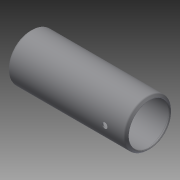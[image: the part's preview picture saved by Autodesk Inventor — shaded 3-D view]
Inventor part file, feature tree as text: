
AUTODESK INVENTOR PART (.ipt)
format: ipt  version: 2014 SP2 (Build 180246200, 246)  size: 158,208 bytes
history: native  units: in
note: dims shown in document units (in); Inventor stores cm internally (conversion verified against a paired STEP export)
features: other x42, sketch x2, revolve x1, extrude x1
ambient origin geometry x8: Origin, YZ Plane, XZ Plane, XY Plane, X Axis, Y Axis, Z Axis, Center Point
bodies: Solid1 (feature_tree)
feature tree (46):
  revolve  "Revolution1"  [1 undecoded]
  extrude  "Extrusion1"  [1 undecoded]
  other  "cp1_XY"
  other  "cp1_YZ"
  other  "cp1_ZX"
  other  "cp1_X"
  other  "cp1_Y"
  other  "cp1_Z"
  other  "cp1_Center"
  other  "cp2_XY"
  other  "cp2_YZ"
  other  "cp2_ZX"
  other  "cp2_X"
  other  "cp2_Y"
  other  "cp2_Z"
  other  "cp2_Center"
  other  "cp3_XY"
  other  "cp3_YZ"
  other  "cp3_ZX"
  other  "cp3_X"
  other  "cp3_Y"
  other  "cp3_Z"
  other  "cp3_Center"
  other  "cp4_XY"
  other  "cp4_YZ"
  other  "cp4_ZX"
  other  "cp4_X"
  other  "cp4_Y"
  other  "cp4_Z"
  other  "cp4_Center"
  other  "tube_front_XY"
  other  "tube_front_YZ"
  other  "tube_front_ZX"
  other  "tube_front_X"
  other  "tube_front_Y"
  other  "tube_front_Z"
  other  "tube_front_Center"
  other  "tube_rear_XY"
  other  "tube_rear_YZ"
  other  "tube_rear_ZX"
  other  "tube_rear_X"
  other  "tube_rear_Y"
  other  "tube_rear_Z"
  other  "tube_rear_Center"
  sketch  "Sketch_1"  dims[d0=360.0deg d1=0.4038in d2=0.0in]
  sketch  "Sketch_7"
note: 2 required parameter values undecoded (feature->parameter linkage not recoverable at this tier; creation-order binding heuristic only, values carry confidence <= 0.55)